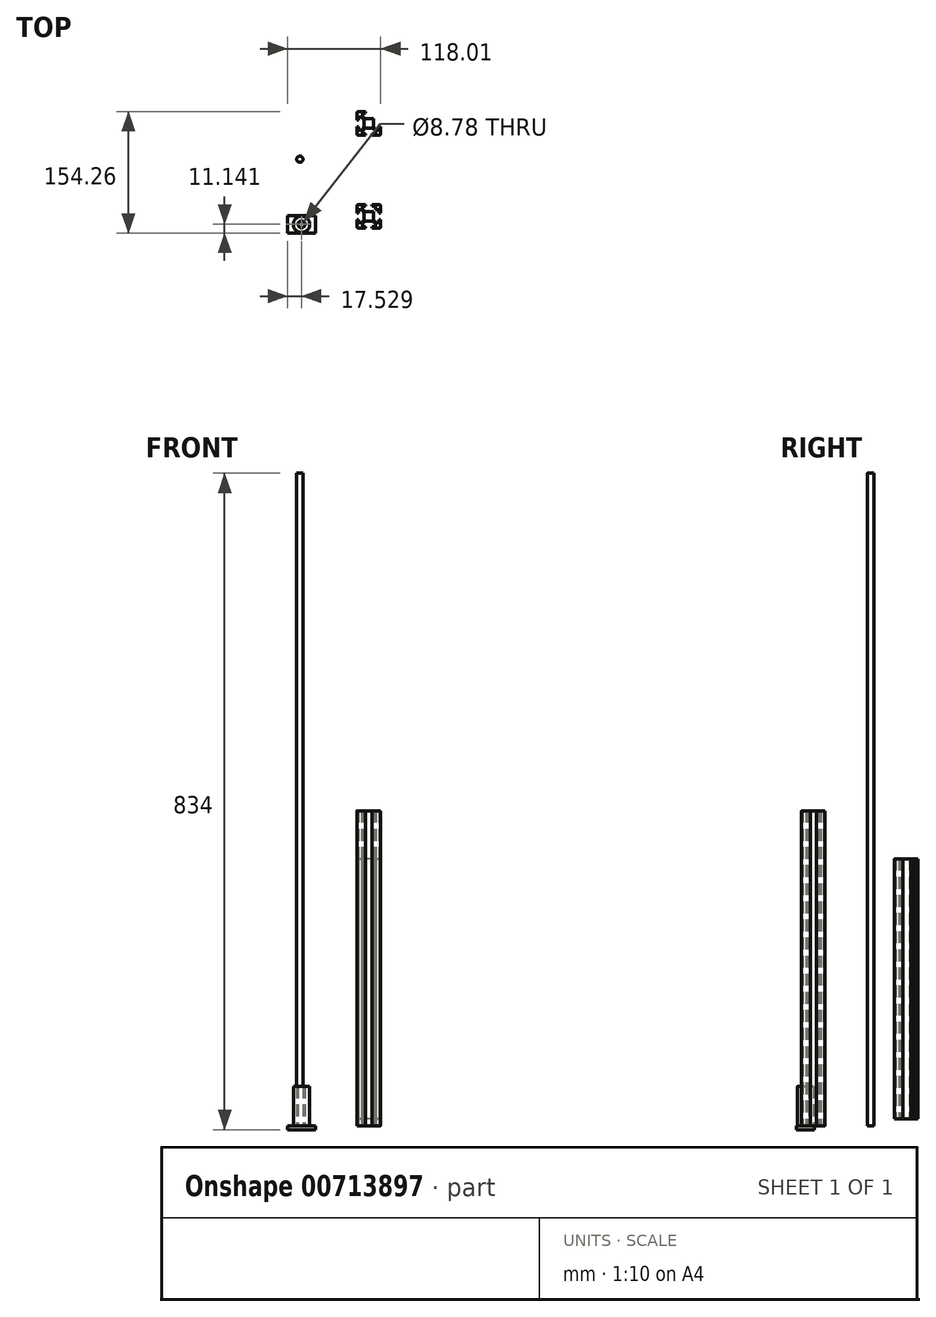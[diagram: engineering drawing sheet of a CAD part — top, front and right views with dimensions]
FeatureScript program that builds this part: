
annotation { "Feature Type Name" : "Feature", "Feature Type Description" : "" }
export const myFeature = defineFeature(function(context is Context, id is Id, definition is map)
    precondition{}
    {
        {
            var Q0;
            Q0=qCreatedBy(makeId("Top.planeOp"),FACE);
            var sketch = newSketch(context, id + "F0", { "sketchPlane" : qUnion([Q0])});
            skPoint(sketch, "E0.middle", {"position": v(42.98, -49.46) * mm});
            skLineSegment(sketch, "E1.bottom", {"start": v(48.98, -55.46) * mm, "end": v(36.98, -55.46) * mm});
            skLineSegment(sketch, "E1.top", {"start": v(48.98, -43.46) * mm, "end": v(36.98, -43.46) * mm});
            skLineSegment(sketch, "E1.left", {"start": v(48.98, -55.46) * mm, "end": v(48.98, -43.46) * mm});
            skLineSegment(sketch, "E1.right", {"start": v(36.98, -55.46) * mm, "end": v(36.98, -43.46) * mm});
            skLineSegment(sketch, "E2.bottom", {"start": v(34.73, -34.45) * mm, "end": v(29.98, -34.45) * mm});
            skLineSegment(sketch, "E2.top", {"start": v(34.73, -41.2) * mm, "end": v(27.98, -41.2) * mm});
            skLineSegment(sketch, "E2.left", {"start": v(34.73, -34.45) * mm, "end": v(34.73, -41.2) * mm});
            skLineSegment(sketch, "E2.right", {"start": v(27.98, -36.45) * mm, "end": v(27.98, -41.2) * mm});
            skPoint(sketch, "E2.middle", {"position": v(31.35, -37.83) * mm});
            skLineSegment(sketch, "E3", {"start": v(34.73, -34.45) * mm, "end": v(38.98, -34.45) * mm});
            skLineSegment(sketch, "E4", {"start": v(38.98, -34.45) * mm, "end": v(38.98, -36.45) * mm});
            skLineSegment(sketch, "E5", {"start": v(38.98, -36.45) * mm, "end": v(34.73, -36.45) * mm});
            skLineSegment(sketch, "E6.bottom", {"start": v(27.98, -41.2) * mm, "end": v(29.98, -41.2) * mm});
            skLineSegment(sketch, "E6.top", {"start": v(27.98, -45.45) * mm, "end": v(29.98, -45.45) * mm});
            skLineSegment(sketch, "E6.left", {"start": v(27.98, -41.2) * mm, "end": v(27.98, -45.45) * mm});
            skLineSegment(sketch, "E6.right", {"start": v(29.98, -41.2) * mm, "end": v(29.98, -45.45) * mm});
            skPoint(sketch, "E7", {"position": v(27.98, -41.2) * mm});
            skPoint(sketch, "E8.visualSharp", {"position": v(27.98, -34.45) * mm});
            skArc(sketch, "E8.filletArc", {"start": v(29.98, -34.45) * mm, "mid": v(28.57, -35.04) * mm, "end": v(27.98, -36.45) * mm});
            skLineSegment(sketch, "E9", {"start": v(34.73, -40) * mm, "end": v(38.06, -43.46) * mm});
            skLineSegment(sketch, "E10", {"start": v(38.06, -43.46) * mm, "end": v(36.53, -41.88) * mm});
            skLineSegment(sketch, "E11", {"start": v(33.49, -41.2) * mm, "end": v(36.98, -44.77) * mm});
            skLineSegment(sketch, "E12.1.0.0", {"start": v(58.03, -45.45) * mm, "end": v(56.03, -45.45) * mm});
            skPoint(sketch, "E12.1.0.1", {"position": v(51.28, -34.45) * mm});
            skLineSegment(sketch, "E12.1.0.2", {"start": v(58.03, -41.2) * mm, "end": v(51.28, -41.2) * mm});
            skLineSegment(sketch, "E12.1.0.3", {"start": v(58.03, -41.2) * mm, "end": v(58.03, -45.45) * mm});
            skArc(sketch, "E12.1.0.4", {"start": v(58.03, -36.45) * mm, "mid": v(57.44, -35.04) * mm, "end": v(56.03, -34.45) * mm});
            skPoint(sketch, "E12.1.0.5", {"position": v(58.03, -34.45) * mm});
            skPoint(sketch, "E12.1.0.6", {"position": v(54.65, -37.82) * mm});
            skLineSegment(sketch, "E12.1.0.7", {"start": v(51.28, -34.45) * mm, "end": v(51.28, -36.45) * mm});
            skLineSegment(sketch, "E12.1.0.8", {"start": v(52.54, -41.2) * mm, "end": v(48.98, -44.62) * mm});
            skLineSegment(sketch, "E12.1.0.9", {"start": v(56.03, -45.45) * mm, "end": v(56.03, -41.2) * mm});
            skLineSegment(sketch, "E12.1.0.10", {"start": v(56.03, -34.45) * mm, "end": v(51.28, -34.45) * mm});
            skLineSegment(sketch, "E12.1.0.11", {"start": v(51.28, -41.2) * mm, "end": v(51.28, -34.45) * mm});
            skLineSegment(sketch, "E12.1.0.12", {"start": v(58.03, -41.2) * mm, "end": v(58.03, -36.45) * mm});
            skLineSegment(sketch, "E12.1.0.13", {"start": v(51.28, -39.96) * mm, "end": v(47.7, -43.46) * mm});
            skLineSegment(sketch, "E12.1.0.15", {"start": v(51.28, -36.45) * mm, "end": v(47.03, -36.45) * mm});
            skLineSegment(sketch, "E12.1.0.16", {"start": v(51.28, -34.45) * mm, "end": v(47.03, -34.45) * mm});
            skLineSegment(sketch, "E12.1.0.17", {"start": v(47.03, -34.45) * mm, "end": v(47.03, -36.45) * mm});
            skPoint(sketch, "E13.1.0.0", {"position": v(57.97, -57.7) * mm});
            skLineSegment(sketch, "E13.1.0.1", {"start": v(57.97, -62.46) * mm, "end": v(57.97, -57.7) * mm});
            skLineSegment(sketch, "E13.1.0.2", {"start": v(57.97, -53.46) * mm, "end": v(55.97, -53.46) * mm});
            skLineSegment(sketch, "E13.1.0.3", {"start": v(57.97, -57.7) * mm, "end": v(57.97, -53.46) * mm});
            skLineSegment(sketch, "E13.1.0.4", {"start": v(57.97, -57.7) * mm, "end": v(55.97, -57.7) * mm});
            skLineSegment(sketch, "E13.1.0.5", {"start": v(51.22, -64.46) * mm, "end": v(51.22, -57.7) * mm});
            skLineSegment(sketch, "E13.1.0.6", {"start": v(52.47, -57.7) * mm, "end": v(48.98, -54.14) * mm});
            skPoint(sketch, "E13.1.0.7", {"position": v(57.97, -64.46) * mm});
            skLineSegment(sketch, "E13.1.0.8", {"start": v(51.22, -57.7) * mm, "end": v(57.97, -57.7) * mm});
            skPoint(sketch, "E13.1.0.9", {"position": v(54.6, -61.08) * mm});
            skLineSegment(sketch, "E13.1.0.10", {"start": v(51.22, -64.46) * mm, "end": v(55.97, -64.46) * mm});
            skLineSegment(sketch, "E13.1.0.11", {"start": v(55.97, -57.7) * mm, "end": v(55.97, -53.46) * mm});
            skArc(sketch, "E13.1.0.12", {"start": v(55.97, -64.46) * mm, "mid": v(57.39, -63.87) * mm, "end": v(57.97, -62.46) * mm});
            skLineSegment(sketch, "E13.1.0.13", {"start": v(51.22, -58.9) * mm, "end": v(47.9, -55.45) * mm});
            skLineSegment(sketch, "E13.1.0.14", {"start": v(46.97, -62.46) * mm, "end": v(51.22, -62.46) * mm});
            skLineSegment(sketch, "E13.1.0.15", {"start": v(51.22, -64.46) * mm, "end": v(46.97, -64.46) * mm});
            skLineSegment(sketch, "E13.1.0.16", {"start": v(46.97, -64.46) * mm, "end": v(46.97, -62.46) * mm});
            skPoint(sketch, "E14.1.0.0", {"position": v(34.75, -64.44) * mm});
            skLineSegment(sketch, "E14.1.0.1", {"start": v(30, -64.44) * mm, "end": v(34.75, -64.44) * mm});
            skLineSegment(sketch, "E14.1.0.2", {"start": v(39, -64.44) * mm, "end": v(39, -62.44) * mm});
            skLineSegment(sketch, "E14.1.0.3", {"start": v(34.75, -64.44) * mm, "end": v(39, -64.44) * mm});
            skLineSegment(sketch, "E14.1.0.4", {"start": v(34.75, -64.44) * mm, "end": v(34.75, -62.44) * mm});
            skLineSegment(sketch, "E14.1.0.5", {"start": v(28, -57.69) * mm, "end": v(34.75, -57.69) * mm});
            skLineSegment(sketch, "E14.1.0.6", {"start": v(34.75, -58.93) * mm, "end": v(38.32, -55.44) * mm});
            skPoint(sketch, "E14.1.0.7", {"position": v(28, -64.44) * mm});
            skLineSegment(sketch, "E14.1.0.8", {"start": v(34.75, -57.69) * mm, "end": v(34.75, -64.44) * mm});
            skPoint(sketch, "E14.1.0.9", {"position": v(31.38, -61.06) * mm});
            skLineSegment(sketch, "E14.1.0.10", {"start": v(28, -57.69) * mm, "end": v(28, -62.44) * mm});
            skLineSegment(sketch, "E14.1.0.11", {"start": v(34.75, -62.44) * mm, "end": v(39, -62.44) * mm});
            skArc(sketch, "E14.1.0.12", {"start": v(28, -62.44) * mm, "mid": v(28.59, -63.85) * mm, "end": v(30, -64.44) * mm});
            skLineSegment(sketch, "E14.1.0.13", {"start": v(33.55, -57.69) * mm, "end": v(37, -54.37) * mm});
            skLineSegment(sketch, "E14.1.0.14", {"start": v(30, -53.44) * mm, "end": v(30, -57.69) * mm});
            skLineSegment(sketch, "E14.1.0.15", {"start": v(28, -57.69) * mm, "end": v(28, -53.44) * mm});
            skLineSegment(sketch, "E14.1.0.16", {"start": v(28, -53.44) * mm, "end": v(30, -53.44) * mm});
            skSolve(sketch);
        }
        {
            var Q0;
            Q0=qCreatedBy(makeId("Right.planeOp"),FACE);
            var sketch = newSketch(context, id + "F1", { "sketchPlane" : qUnion([Q0])});
            skLineSegment(sketch, "E15", {"start": v(3.3, 0) * mm, "end": v(43.42, 0) * mm});
            skLineSegment(sketch, "E16", {"start": v(3.3, 0) * mm, "end": v(3.3, 40.11) * mm});
            skLineSegment(sketch, "E17", {"start": v(3.3, 40.11) * mm, "end": v(43.42, 0) * mm});
            skSolve(sketch);
        }
        {
            var Q0;
            Q0=qSketchRegion(id+"F0",true);
            extrude(context, id + "F2", {"entities" : qUnion([Q0]), "depth" : 400 * mm, "offsetDistance" : 25 * mm});
        }
        {
            var Q0;
            Q0=makeQuery(id+"F1.imprint","IMPRINT",FACE,{"disambiguationData":[TD([[makeQuery(id+"F1.imprint","IMPRINT",EDGE,{"derivedFrom":sQuery(id+"F1.wireOp",EDGE,"E15")}),1.0]])]});
            extrude(context, id + "F3", {"entities" : qUnion([Q0]), "depth" : 30 * mm, "offsetDistance" : 25 * mm});
        }
        {
            var Q0;
            Q0=makeQuery(id+"F3.opExtrude","SWEPT_FACE",FACE,{"disambiguationData":[OSD([sQuery(id+"F1.wireOp",EDGE,"E17")])]});
            shell(context, id + "F4", {"entities" : qUnion([Q0]), "thickness" : 5 * mm});
        }
        {
            var Q0;
            Q0=makeQuery(id+"F3.opExtrude","SWEPT_BODY",BODY,{"disambiguationData":[OSD([sQuery(id+"F1.wireOp",EDGE,"E15"),sQuery(id+"F1.wireOp",EDGE,"E16"),sQuery(id+"F1.wireOp",EDGE,"E17")])]});
            deleteBodies(context, id + "F5", {"entities" : qUnion([Q0])});
        }
        {
            var Q0;
            Q0=makeQuery(id+"F2.opExtrude","CAP_FACE",FACE,{"disambiguationData":[OSD([sQuery(id+"F0.wireOp",EDGE,"E1.bottom"),sQuery(id+"F0.wireOp",EDGE,"E1.top"),sQuery(id+"F0.wireOp",EDGE,"E1.left"),sQuery(id+"F0.wireOp",EDGE,"E1.right"),sQuery(id+"F0.wireOp",EDGE,"E2.bottom"),sQuery(id+"F0.wireOp",EDGE,"E2.top"),sQuery(id+"F0.wireOp",EDGE,"E2.left"),sQuery(id+"F0.wireOp",EDGE,"E2.right"),sQuery(id+"F0.wireOp",EDGE,"E3"),sQuery(id+"F0.wireOp",EDGE,"E4"),sQuery(id+"F0.wireOp",EDGE,"E5"),sQuery(id+"F0.wireOp",EDGE,"E6.top"),sQuery(id+"F0.wireOp",EDGE,"E6.left"),sQuery(id+"F0.wireOp",EDGE,"E6.right"),sQuery(id+"F0.wireOp",EDGE,"E8.filletArc"),sQuery(id+"F0.wireOp",EDGE,"E9"),sQuery(id+"F0.wireOp",EDGE,"E10"),sQuery(id+"F0.wireOp",EDGE,"E11"),sQuery(id+"F0.wireOp",EDGE,"E12.1.0.0"),sQuery(id+"F0.wireOp",EDGE,"E12.1.0.2"),sQuery(id+"F0.wireOp",EDGE,"E12.1.0.3"),sQuery(id+"F0.wireOp",EDGE,"E12.1.0.4"),sQuery(id+"F0.wireOp",EDGE,"E12.1.0.8"),sQuery(id+"F0.wireOp",EDGE,"E12.1.0.9"),sQuery(id+"F0.wireOp",EDGE,"E12.1.0.10"),sQuery(id+"F0.wireOp",EDGE,"E12.1.0.11"),sQuery(id+"F0.wireOp",EDGE,"E12.1.0.12"),sQuery(id+"F0.wireOp",EDGE,"E12.1.0.13"),sQuery(id+"F0.wireOp",EDGE,"E12.1.0.15"),sQuery(id+"F0.wireOp",EDGE,"E12.1.0.16"),sQuery(id+"F0.wireOp",EDGE,"E12.1.0.17"),sQuery(id+"F0.wireOp",EDGE,"E13.1.0.1"),sQuery(id+"F0.wireOp",EDGE,"E13.1.0.2"),sQuery(id+"F0.wireOp",EDGE,"E13.1.0.3"),sQuery(id+"F0.wireOp",EDGE,"E13.1.0.5"),sQuery(id+"F0.wireOp",EDGE,"E13.1.0.6"),sQuery(id+"F0.wireOp",EDGE,"E13.1.0.8"),sQuery(id+"F0.wireOp",EDGE,"E13.1.0.10"),sQuery(id+"F0.wireOp",EDGE,"E13.1.0.11"),sQuery(id+"F0.wireOp",EDGE,"E13.1.0.12"),sQuery(id+"F0.wireOp",EDGE,"E13.1.0.13"),sQuery(id+"F0.wireOp",EDGE,"E13.1.0.14"),sQuery(id+"F0.wireOp",EDGE,"E13.1.0.15"),sQuery(id+"F0.wireOp",EDGE,"E13.1.0.16"),sQuery(id+"F0.wireOp",EDGE,"E14.1.0.1"),sQuery(id+"F0.wireOp",EDGE,"E14.1.0.2"),sQuery(id+"F0.wireOp",EDGE,"E14.1.0.3"),sQuery(id+"F0.wireOp",EDGE,"E14.1.0.5"),sQuery(id+"F0.wireOp",EDGE,"E14.1.0.6"),sQuery(id+"F0.wireOp",EDGE,"E14.1.0.8"),sQuery(id+"F0.wireOp",EDGE,"E14.1.0.10"),sQuery(id+"F0.wireOp",EDGE,"E14.1.0.11"),sQuery(id+"F0.wireOp",EDGE,"E14.1.0.12"),sQuery(id+"F0.wireOp",EDGE,"E14.1.0.13"),sQuery(id+"F0.wireOp",EDGE,"E14.1.0.14"),sQuery(id+"F0.wireOp",EDGE,"E14.1.0.15"),sQuery(id+"F0.wireOp",EDGE,"E14.1.0.16")])],"isStart":false});
            extrude(context, id + "F6", {"entities" : qUnion([Q0]), "depth" : 330 * mm, "offsetDistance" : 25 * mm});
        }
        {
            var Q0;
            Q0=qCreatedBy(makeId("Top.planeOp"),FACE);
            var sketch = newSketch(context, id + "F7", { "sketchPlane" : qUnion([Q0])});
            skCircle(sketch, "E18", {"center": v(-44.6, 23.17) * mm, "radius": 4.01 * mm});
            skSolve(sketch);
        }
        {
            var Q0;
            Q0=makeQuery(id+"F7.imprint","IMPRINT",FACE,{"disambiguationData":[TD([[makeQuery(id+"F7.imprint","IMPRINT",EDGE,{"derivedFrom":sQuery(id+"F7.wireOp",EDGE,"E18")}),1.0]])]});
            extrude(context, id + "F8", {"entities" : qUnion([Q0]), "depth" : 829 * mm, "offsetDistance" : 25 * mm});
        }
        {
            var Q0;
            Q0=makeQuery(id+"F6.opExtrude","SWEPT_BODY",BODY,{"disambiguationData":[OSD([sQuery(id+"F0.wireOp",EDGE,"E1.bottom"),sQuery(id+"F0.wireOp",EDGE,"E1.top"),sQuery(id+"F0.wireOp",EDGE,"E1.left"),sQuery(id+"F0.wireOp",EDGE,"E1.right"),sQuery(id+"F0.wireOp",EDGE,"E2.bottom"),sQuery(id+"F0.wireOp",EDGE,"E2.top"),sQuery(id+"F0.wireOp",EDGE,"E2.left"),sQuery(id+"F0.wireOp",EDGE,"E2.right"),sQuery(id+"F0.wireOp",EDGE,"E3"),sQuery(id+"F0.wireOp",EDGE,"E4"),sQuery(id+"F0.wireOp",EDGE,"E5"),sQuery(id+"F0.wireOp",EDGE,"E6.top"),sQuery(id+"F0.wireOp",EDGE,"E6.left"),sQuery(id+"F0.wireOp",EDGE,"E6.right"),sQuery(id+"F0.wireOp",EDGE,"E8.filletArc"),sQuery(id+"F0.wireOp",EDGE,"E9"),sQuery(id+"F0.wireOp",EDGE,"E10"),sQuery(id+"F0.wireOp",EDGE,"E11"),sQuery(id+"F0.wireOp",EDGE,"E12.1.0.0"),sQuery(id+"F0.wireOp",EDGE,"E12.1.0.2"),sQuery(id+"F0.wireOp",EDGE,"E12.1.0.3"),sQuery(id+"F0.wireOp",EDGE,"E12.1.0.4"),sQuery(id+"F0.wireOp",EDGE,"E12.1.0.8"),sQuery(id+"F0.wireOp",EDGE,"E12.1.0.9"),sQuery(id+"F0.wireOp",EDGE,"E12.1.0.10"),sQuery(id+"F0.wireOp",EDGE,"E12.1.0.11"),sQuery(id+"F0.wireOp",EDGE,"E12.1.0.12"),sQuery(id+"F0.wireOp",EDGE,"E12.1.0.13"),sQuery(id+"F0.wireOp",EDGE,"E12.1.0.15"),sQuery(id+"F0.wireOp",EDGE,"E12.1.0.16"),sQuery(id+"F0.wireOp",EDGE,"E12.1.0.17"),sQuery(id+"F0.wireOp",EDGE,"E13.1.0.1"),sQuery(id+"F0.wireOp",EDGE,"E13.1.0.2"),sQuery(id+"F0.wireOp",EDGE,"E13.1.0.3"),sQuery(id+"F0.wireOp",EDGE,"E13.1.0.5"),sQuery(id+"F0.wireOp",EDGE,"E13.1.0.6"),sQuery(id+"F0.wireOp",EDGE,"E13.1.0.8"),sQuery(id+"F0.wireOp",EDGE,"E13.1.0.10"),sQuery(id+"F0.wireOp",EDGE,"E13.1.0.11"),sQuery(id+"F0.wireOp",EDGE,"E13.1.0.12"),sQuery(id+"F0.wireOp",EDGE,"E13.1.0.13"),sQuery(id+"F0.wireOp",EDGE,"E13.1.0.14"),sQuery(id+"F0.wireOp",EDGE,"E13.1.0.15"),sQuery(id+"F0.wireOp",EDGE,"E13.1.0.16"),sQuery(id+"F0.wireOp",EDGE,"E14.1.0.1"),sQuery(id+"F0.wireOp",EDGE,"E14.1.0.2"),sQuery(id+"F0.wireOp",EDGE,"E14.1.0.3"),sQuery(id+"F0.wireOp",EDGE,"E14.1.0.5"),sQuery(id+"F0.wireOp",EDGE,"E14.1.0.6"),sQuery(id+"F0.wireOp",EDGE,"E14.1.0.8"),sQuery(id+"F0.wireOp",EDGE,"E14.1.0.10"),sQuery(id+"F0.wireOp",EDGE,"E14.1.0.11"),sQuery(id+"F0.wireOp",EDGE,"E14.1.0.12"),sQuery(id+"F0.wireOp",EDGE,"E14.1.0.13"),sQuery(id+"F0.wireOp",EDGE,"E14.1.0.14"),sQuery(id+"F0.wireOp",EDGE,"E14.1.0.15"),sQuery(id+"F0.wireOp",EDGE,"E14.1.0.16")])]});
            transform(context, id + "F9", {"entities" : qUnion([Q0]), "transformType" : TransformType.TRANSLATION_3D, "dx" : 0 * mm, "dy" : 118 * mm, "dz" : -391 * mm, "makeCopy" : false});
        }
        {
            var Q0;
            Q0=qCreatedBy(makeId("Top.planeOp"),FACE);
            var sketch = newSketch(context, id + "F10", { "sketchPlane" : qUnion([Q0])});
            skCircle(sketch, "E19", {"center": v(-42.45, -59.57) * mm, "radius": 10.41 * mm});
            skCircle(sketch, "E20", {"center": v(-42.45, -59.57) * mm, "radius": 4.39 * mm});
            skSolve(sketch);
        }
        {
            var Q0;
            Q0 = qSketchRegion(id + "F10", true);
            extrude(context, id + "F11", {"entities" : qUnion([Q0]), "depth" : 50 * mm, "offsetDistance" : 25 * mm});
        }
        {
            var Q0;
            Q0=qCreatedBy(makeId("Top.planeOp"),FACE);
            var sketch = newSketch(context, id + "F12", { "sketchPlane" : qUnion([Q0])});
            skLineSegment(sketch, "E21.bottom", {"start": v(-24.72, -48.27) * mm, "end": v(-59.98, -48.27) * mm});
            skLineSegment(sketch, "E21.top", {"start": v(-24.72, -70.71) * mm, "end": v(-59.98, -70.71) * mm});
            skLineSegment(sketch, "E21.left", {"start": v(-24.72, -48.27) * mm, "end": v(-24.72, -70.71) * mm});
            skLineSegment(sketch, "E21.right", {"start": v(-59.98, -48.27) * mm, "end": v(-59.98, -70.71) * mm});
            skPoint(sketch, "E21.middle", {"position": v(-42.35, -59.5) * mm});
            skSolve(sketch);
        }
        {
            var Q0;
            Q0=makeQuery(id+"F12.imprint","IMPRINT",FACE,{"disambiguationData":[TD([[makeQuery(id+"F12.imprint","IMPRINT",EDGE,{"derivedFrom":sQuery(id+"F12.wireOp",EDGE,"E21.bottom")}),1.0]])]});
            extrude(context, id + "F13", {"entities" : qUnion([Q0]), "oppositeDirection" : true, "depth" : 5 * mm, "offsetDistance" : 25 * mm});
        }
        {
            var Q0;
            Q0=makeQuery(id+"F8.opExtrude","SWEPT_BODY",BODY,{"disambiguationData":[OSD([sQuery(id+"F7.wireOp",EDGE,"E18")])]});
            transform(context, id + "F14", {"entities" : qUnion([Q0]), "transformType" : TransformType.TRANSLATION_3D, "dx" : 2.1 * mm, "dy" : -82.7 * mm, "dz" : 0 * mm, "makeCopy" : true});
        }
        {
            var Q0;
            Q0=makeQuery(id+"F14.opPattern","COPY",BODY,{"derivedFrom":makeQuery(id+"F8.opExtrude","SWEPT_BODY",BODY,{"disambiguationData":[OSD([sQuery(id+"F7.wireOp",EDGE,"E18")])]}),"instanceName":"1"});
            transform(context, id + "F15", {"entities" : qUnion([Q0]), "transformType" : TransformType.TRANSLATION_3D, "dx" : 0 * mm, "dy" : 0 * mm, "dz" : -122 * mm, "makeCopy" : false});
        }
        {
            var Q0;
            Q0=makeQuery(id+"F14.opPattern","COPY",BODY,{"derivedFrom":makeQuery(id+"F8.opExtrude","SWEPT_BODY",BODY,{"disambiguationData":[OSD([sQuery(id+"F7.wireOp",EDGE,"E18")])]}),"instanceName":"1"});
            var Q1;
            Q1=makeQuery(id+"F11.opExtrude","SWEPT_BODY",BODY,{"disambiguationData":[OSD([sQuery(id+"F10.wireOp",EDGE,"E19"),sQuery(id+"F10.wireOp",EDGE,"E20")])]});
            booleanBodies(context, id + "F16", {"operationType" : BooleanOperationType.SUBTRACTION, "tools" : qUnion([Q0]), "targets" : qUnion([Q1])});
        }
    });
